# Revit family: Barrier_Gate_AutoGate_Chainlink-BarbedTop
name_source: partatom
category: Generic Models
revit_build: Autodesk Revit 2015 (Build: 20140606_1530(x64)
units: mm (PartAtom-declared; Revit-internal decimal feet)

## types (1)
- Size as Specified
    Construction Details = http://www.arcat.com
    Decorative Channel Height = 1' - 0"
    Default Elevation = 0' - 0"
    Description = AutoGate Chain Link Gate as Specified
    Expected Lifespan (Years) = 0
    Maintenance Schedule (Months) = 0
    Manufacturer = AutoGate, Inc
    Manufacturer Fax = 419-588-3514
    Manufacturer Website = http://autogate.com
    Maximum Size = as Specified
    Model = Chain Link with Barbed Top
    Number of Inner Design Repeats = 3
    Product Data = http://www.arcat.com
    Revision = R1_2016-11
    Sales Information = http://autogate.com
    Specification = http://www.arcat.com
    URL = http://autogate.com
    Warranty Duration (Years) = 0

## geometry (parser evidence)
native form markers: Sweep x6
no freeform markers — native parametric forms only
